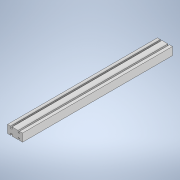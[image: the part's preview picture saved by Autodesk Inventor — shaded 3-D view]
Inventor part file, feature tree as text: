
AUTODESK INVENTOR PART (.ipt)
format: ipt  version: 2022 (Build 260153000, 153)  size: 128,512 bytes
history: native  units: in
note: dims shown in document units (in); Inventor stores cm internally (conversion verified against a paired STEP export)
features: extrude x2, sketch x2, mirror x1
ambient origin geometry x8: Origin, YZ Plane, XZ Plane, XY Plane, X Axis, Y Axis, Z Axis, Center Point
bodies: Solid1 (feature_tree)
feature tree (5):
  extrude  "Extrusion1"  Depth=15.6693in
  extrude  "Extrusion2"  Depth=0.1575in
  mirror  "Mirror1"
  sketch  "Sketch1"  dims[d0=1.5709in d1=15.6693in]
  sketch  "Sketch2"  dims[d2=0.8268in d3=0.0in d4=0.1575in d5=0.315in d6=0.1969in d7=0.0in]
